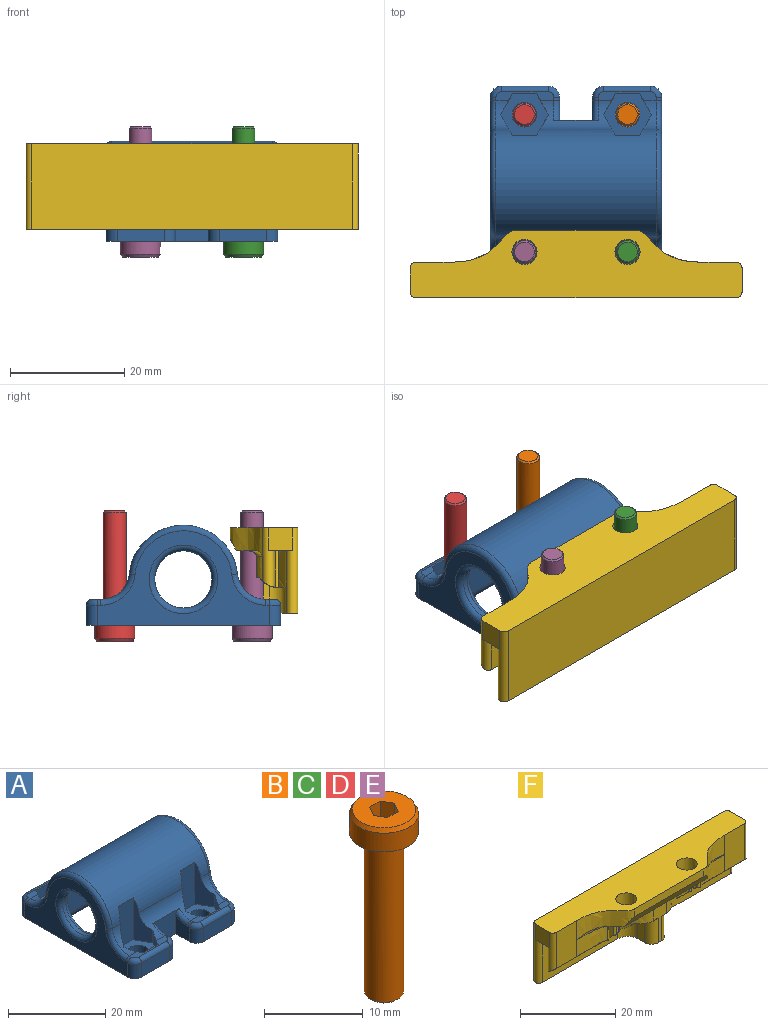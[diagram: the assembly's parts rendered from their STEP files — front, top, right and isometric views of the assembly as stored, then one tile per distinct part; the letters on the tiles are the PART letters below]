
ASSEMBLY  parts=6 mates=5
PART A: 114 faces, bbox 30.4x34.4x18.3 mm
  f0: cylinder r=2.15mm len=4.3mm, axis (0,0,-1), area 27mm2, adj f21,f94
  f1: cylinder r=2.15mm len=4.3mm, axis (0,0,-1), area 27mm2, adj f21,f95
  f2: cylinder r=2.15mm len=4.3mm, axis (0,0,-1), area 27mm2, adj f21,f108
  f3: cylinder r=2.15mm len=4.3mm, axis (0,0,-1), area 27mm2, adj f21,f81
  f4: cylinder r=5mm len=4.97mm, axis (-1,0,0), area 11.9mm2, adj f20,f22,f55,f103,f104
  f5: cylinder r=5mm len=4.97mm, axis (-1,0,0), area 11.9mm2, adj f9,f22,f70,f97,f98
  f6: cylinder r=5mm len=4.97mm, axis (-1,0,0), area 11.9mm2, adj f16,f22,f68,f89,f90
  f7: cylinder r=5mm len=4.97mm, axis (-1,0,0), area 11.9mm2, adj f8,f22,f53,f83,f84
  f8: plane 10.15x1.58mm, normal (0,0,1), area 9.5mm2, adj f7,f46,f48,f49,f50,f51,f52,f84
  f9: plane 10.15x1.58mm, normal (0,0,1), area 9.5mm2, adj f5,f45,f71,f72,f73,f74,f75,f98
  f10: plane 8.15x3.5mm, normal (0,-1,0), area 28.5mm2, adj f21,f33,f42,f73
  f11: plane 8.15x3.5mm, normal (0,1,0), area 28.5mm2, adj f21,f36,f43,f65
  f12: plane 24.2x6mm, normal (0,1,0), area 145.2mm2, adj f14,f24,f26,f39
  f13: plane 24.2x6mm, normal (0,-1,0), area 145.2mm2, adj f14,f24,f26,f38
  f14: cylinder r=7.55mm len=24.2mm, axis (-1,0,0), area 446.8mm2, adj f12,f13,f24,f26,f109,f110,f112,f113
  f15: plane 30x16.5mm, normal (-1,0,0), area 196.5mm2, adj f21,f41,f44,f52,f53,f54,f55,f56
  f16: plane 10.15x1.58mm, normal (0,0,1), area 9.5mm2, adj f6,f46,f63,f64,f65,f66,f67,f90
  f17: plane 8.15x3.5mm, normal (0,-1,0), area 28.5mm2, adj f21,f34,f41,f58
  f18: plane 30x16.5mm, normal (1,0,0), area 196.5mm2, adj f21,f42,f43,f67,f68,f69,f70,f71
  f19: plane 8.15x3.5mm, normal (0,1,0), area 28.5mm2, adj f21,f35,f44,f50
  f20: plane 10.15x1.58mm, normal (0,0,1), area 9.5mm2, adj f4,f45,f56,f57,f58,f59,f60,f104
  f21: plane 34x30mm, normal (0,0,-1), area 348mm2, adj f0,f1,f2,f3,f10,f11,f15,f17
  f22: cylinder r=9.5mm len=28mm, axis (-1,0,0), area 706mm2, adj f4,f5,f6,f7,f45,f46,f54,f69
  f23: cylinder r=5mm len=10mm, axis (-1,0,0), area 28.3mm2, adj f79,f80
  f24: plane 15.1x13.55mm, normal (1,0,0), area 67mm2, adj f12,f13,f14,f37,f80
  f25: cylinder r=5mm len=10mm, axis (1,0,0), area 28.3mm2, adj f77,f78
  f26: plane 15.1x13.55mm, normal (-1,0,0), area 67mm2, adj f12,f13,f14,f40,f77
  f27: plane 4.57x4mm, normal (-1,0,0), area 15.2mm2, adj f21,f28,f33,f75,f76
  f28: plane 7.7x5.85mm, normal (0,-1,0), area 33.9mm2, adj f21,f27,f29,f45,f61,f76
  f29: plane 4.57x4mm, normal (1,0,0), area 15.2mm2, adj f21,f28,f34,f60,f61
  f30: plane 4.57x4mm, normal (1,0,0), area 15.2mm2, adj f21,f31,f35,f47,f48
  f31: plane 7.7x5.85mm, normal (0,1,0), area 33.9mm2, adj f21,f30,f32,f46,f47,f62
  f32: plane 4.57x4mm, normal (-1,0,0), area 15.2mm2, adj f21,f31,f36,f62,f63
  f33: cylinder r=2mm len=3.5mm, axis (0,0,1), area 11mm2, adj f10,f21,f27,f74
  f34: cylinder r=2mm len=3.5mm, axis (0,0,-1), area 11mm2, adj f17,f21,f29,f59
  f35: cylinder r=2mm len=3.5mm, axis (0,0,-1), area 11mm2, adj f19,f21,f30,f49
  f36: cylinder r=2mm len=3.5mm, axis (0,0,1), area 11mm2, adj f11,f21,f32,f64
  f37: cylinder r=2mm len=19.1mm, axis (0,-1,0), area 52mm2, adj f21,f24,f38,f39
  f38: cylinder r=2mm len=28.2mm, axis (-1,0,0), area 80.6mm2, adj f13,f21,f37,f40
  f39: cylinder r=2mm len=28.2mm, axis (1,0,0), area 80.6mm2, adj f12,f21,f37,f40
  f40: cylinder r=2mm len=19.1mm, axis (0,-1,0), area 52mm2, adj f21,f26,f38,f39
  f41: cylinder r=2mm len=3.5mm, axis (0,0,-1), area 11mm2, adj f15,f17,f21,f57
  f42: cylinder r=2mm len=3.5mm, axis (0,0,1), area 11mm2, adj f10,f18,f21,f72
  f43: cylinder r=2mm len=3.5mm, axis (0,0,-1), area 11mm2, adj f11,f18,f21,f66
  f44: cylinder r=2mm len=3.5mm, axis (0,0,1), area 11mm2, adj f15,f19,f21,f51
  f45: cylinder r=5mm len=12.52mm, axis (-1,0,0), area 53.5mm2, adj f9,f20,f22,f28,f61,f76,f100,f101
  f46: cylinder r=5mm len=12.52mm, axis (-1,0,0), area 53.5mm2, adj f8,f16,f22,f31,f47,f62,f86,f87
  f47: torus R=6mm, axis (-1,0,0), area 5.8mm2, adj f30,f31,f46,f48
  f48: cylinder r=1mm len=1mm, axis (0,1,0), area 0.9mm2, adj f8,f30,f47,f49
  f49: torus R=1mm, axis (0,0,1), area 4mm2, adj f8,f35,f48,f50
  f50: cylinder r=1mm len=8.15mm, axis (1,0,0), area 12.8mm2, adj f8,f19,f49,f51
  f51: torus R=1mm, axis (0,0,1), area 4mm2, adj f8,f44,f50,f52
  f52: cylinder r=1mm len=1mm, axis (0,1,0), area 0.9mm2, adj f8,f15,f51,f53
  f53: torus R=6mm, axis (1,0,0), area 12.4mm2, adj f7,f15,f52,f54
  f54: torus R=8.5mm, axis (1,0,0), area 42.1mm2, adj f15,f22,f53,f55
  f55: torus R=6mm, axis (1,0,0), area 12.4mm2, adj f4,f15,f54,f56
  f56: cylinder r=1mm len=1mm, axis (0,1,0), area 0.9mm2, adj f15,f20,f55,f57
  f57: torus R=1mm, axis (0,0,1), area 4mm2, adj f20,f41,f56,f58
  f58: cylinder r=1mm len=8.15mm, axis (-1,0,0), area 12.8mm2, adj f17,f20,f57,f59
  f59: torus R=1mm, axis (0,0,1), area 4mm2, adj f20,f34,f58,f60
  f60: cylinder r=1mm len=1mm, axis (0,1,0), area 0.9mm2, adj f20,f29,f59,f61
  f61: torus R=6mm, axis (1,0,0), area 5.8mm2, adj f28,f29,f45,f60
  f62: torus R=6mm, axis (-1,0,0), area 5.8mm2, adj f31,f32,f46,f63
  f63: cylinder r=1mm len=1mm, axis (0,-1,0), area 0.9mm2, adj f16,f32,f62,f64
  f64: torus R=1mm, axis (0,0,1), area 4mm2, adj f16,f36,f63,f65
  f65: cylinder r=1mm len=8.15mm, axis (1,0,0), area 12.8mm2, adj f11,f16,f64,f66
  f66: torus R=1mm, axis (0,0,1), area 4mm2, adj f16,f43,f65,f67
  f67: cylinder r=1mm len=1mm, axis (0,-1,0), area 0.9mm2, adj f16,f18,f66,f68
  f68: torus R=6mm, axis (1,0,0), area 12.4mm2, adj f6,f18,f67,f69
  f69: torus R=8.5mm, axis (1,0,0), area 42.1mm2, adj f18,f22,f68,f70
  f70: torus R=6mm, axis (1,0,0), area 12.4mm2, adj f5,f18,f69,f71
  f71: cylinder r=1mm len=1mm, axis (0,-1,0), area 0.9mm2, adj f9,f18,f70,f72
  f72: torus R=1mm, axis (0,0,1), area 4mm2, adj f9,f42,f71,f73
  f73: cylinder r=1mm len=8.15mm, axis (-1,0,0), area 12.8mm2, adj f9,f10,f72,f74
  f74: torus R=1mm, axis (0,0,1), area 4mm2, adj f9,f33,f73,f75
  f75: cylinder r=1mm len=1mm, axis (0,-1,0), area 0.9mm2, adj f9,f27,f74,f76
  f76: torus R=6mm, axis (1,0,0), area 5.8mm2, adj f27,f28,f45,f75
  f77: torus R=6mm, axis (1,0,0), area 52.9mm2, adj f25,f26
  f78: torus R=6mm, axis (1,0,0), area 52.9mm2, adj f18,f25
  f79: torus R=6mm, axis (1,0,0), area 52.9mm2, adj f15,f23
  f80: torus R=6mm, axis (-1,0,0), area 52.9mm2, adj f23,f24
  f81: plane 8.43x7.3mm, normal (0,0,1), area 31.6mm2, adj f3,f82,f83,f84,f85,f86,f87
  f82: plane 10.53x4.21mm, normal (0,1,0), area 44.4mm2, adj f22,f81,f83,f87
  f83: plane 10.53x3.65mm, normal (0.87,0.5,0), area 24.5mm2, adj f7,f22,f81,f82,f84
  f84: plane 3.7x3.17mm, normal (0.87,-0.5,0), area 11.1mm2, adj f7,f8,f81,f83,f85
  f85: plane 4.21x2.5mm, normal (0,-1,0), area 10.5mm2, adj f8,f81,f84,f86
  f86: plane 3.7x3.17mm, normal (-0.87,-0.5,0), area 11.1mm2, adj f8,f46,f81,f85,f87
  f87: plane 10.53x3.65mm, normal (-0.87,0.5,0), area 24.5mm2, adj f22,f46,f81,f82,f86
  f88: plane 10.53x4.21mm, normal (0,1,0), area 44.4mm2, adj f22,f89,f93,f94
  f89: plane 10.53x3.65mm, normal (-0.87,0.5,0), area 24.5mm2, adj f6,f22,f88,f90,f94
  f90: plane 3.7x3.17mm, normal (-0.87,-0.5,0), area 11.1mm2, adj f6,f16,f89,f91,f94
  f91: plane 4.21x2.5mm, normal (0,-1,0), area 10.5mm2, adj f16,f90,f92,f94
  f92: plane 3.7x3.17mm, normal (0.87,-0.5,0), area 11.1mm2, adj f16,f46,f91,f93,f94
  f93: plane 10.53x3.65mm, normal (0.87,0.5,0), area 24.5mm2, adj f22,f46,f88,f92,f94
  f94: plane 8.43x7.3mm, normal (0,0,1), area 31.6mm2, adj f0,f88,f89,f90,f91,f92,f93
  f95: plane 8.43x7.3mm, normal (0,0,1), area 31.6mm2, adj f1,f96,f97,f98,f99,f100,f101
  f96: plane 10.53x4.21mm, normal (0,-1,0), area 44.4mm2, adj f22,f95,f97,f101
  f97: plane 10.53x3.65mm, normal (-0.87,-0.5,0), area 24.5mm2, adj f5,f22,f95,f96,f98
  f98: plane 3.7x3.17mm, normal (-0.87,0.5,0), area 11.1mm2, adj f5,f9,f95,f97,f99
  f99: plane 4.21x2.5mm, normal (0,1,0), area 10.5mm2, adj f9,f95,f98,f100
  f100: plane 3.7x3.17mm, normal (0.87,0.5,0), area 11.1mm2, adj f9,f45,f95,f99,f101
  f101: plane 10.53x3.65mm, normal (0.87,-0.5,0), area 24.5mm2, adj f22,f45,f95,f96,f100
  f102: plane 10.53x4.21mm, normal (0,-1,0), area 44.4mm2, adj f22,f103,f107,f108
  f103: plane 10.53x3.65mm, normal (0.87,-0.5,0), area 24.5mm2, adj f4,f22,f102,f104,f108
  f104: plane 3.7x3.17mm, normal (0.87,0.5,0), area 11.1mm2, adj f4,f20,f103,f105,f108
  f105: plane 4.21x2.5mm, normal (0,1,0), area 10.5mm2, adj f20,f104,f106,f108
  f106: plane 3.7x3.17mm, normal (-0.87,0.5,0), area 11.1mm2, adj f20,f45,f105,f107,f108
  f107: plane 10.53x3.65mm, normal (-0.87,-0.5,0), area 24.5mm2, adj f22,f45,f102,f106,f108
  f108: plane 8.43x7.3mm, normal (0,0,1), area 31.6mm2, adj f2,f102,f103,f104,f105,f106,f107
  f109: plane 5.64x1mm, normal (1,0,0), area 2.9mm2, adj f14,f111,f112,f113
  f110: plane 5.64x1mm, normal (-1,0,0), area 2.9mm2, adj f14,f111,f112,f113
  f111: plane 22x4.3mm, normal (0,0,-1), area 94.5mm2, adj f109,f110,f112,f113
  f112: plane 22x1mm, normal (0,-0.83,-0.56), area 26.5mm2, adj f14,f109,f110,f111
  f113: plane 22x1mm, normal (0,0.83,-0.56), area 26.5mm2, adj f14,f109,f110,f111
PART B: 19 faces, bbox 7x7x22.8 mm
  f0: plane 6.43x6.43mm, normal (0,0,1), area 26.7mm2, adj f3,f10,f11,f12,f13,f14,f15
  f1: cylinder r=3.5mm len=7mm, axis (0,0,-1), area 50.8mm2, adj f2,f3
  f2: plane 7x7mm, normal (0,0,-1), area 26mm2, adj f1,f16
  f3: cone r=3.5mm half-angle=30deg, axis (0,0,-1), area 11.9mm2, adj f0,f1
  f4: plane 1.5x1.3mm, normal (-0.15,0.09,0.98), area 1mm2, adj f5,f9,f12
  f5: plane 1.5x1.3mm, normal (0,0.17,0.98), area 1mm2, adj f4,f6,f13
  f6: plane 1.5x1.3mm, normal (0.15,0.09,0.98), area 1mm2, adj f5,f7,f14
  f7: plane 1.5x1.3mm, normal (0.15,-0.09,0.98), area 1mm2, adj f6,f8,f15
  f8: plane 1.5x1.3mm, normal (0,-0.17,0.98), area 1mm2, adj f7,f9,f10
  f9: plane 1.5x1.3mm, normal (-0.15,-0.09,0.98), area 1mm2, adj f4,f8,f11
  f10: plane 2.3x1.5mm, normal (0,-1,0), area 3.4mm2, adj f0,f8,f11,f15
  f11: plane 2.3x1.3mm, normal (-0.87,-0.5,0), area 3.4mm2, adj f0,f9,f10,f12
  f12: plane 2.3x1.3mm, normal (-0.87,0.5,0), area 3.4mm2, adj f0,f4,f11,f13
  f13: plane 2.3x1.5mm, normal (0,1,0), area 3.4mm2, adj f0,f5,f12,f14
  f14: plane 2.3x1.3mm, normal (0.87,0.5,0), area 3.4mm2, adj f0,f6,f13,f15
  f15: plane 2.3x1.3mm, normal (0.87,-0.5,0), area 3.4mm2, adj f0,f7,f10,f14
  f16: cylinder r=1.99mm len=19.72mm, axis (0,0,1), area 246.6mm2, adj f2,f18
  f17: plane 3.42x3.42mm, normal (0,0,-1), area 9.2mm2, adj f18
  f18: cone r=1.71mm half-angle=45deg, axis (0,0,1), area 4.6mm2, adj f16,f17
PART C: same geometry as B
PART D: same geometry as B
PART E: same geometry as B
PART F: 67 faces, bbox 58.7x12.7x15.7 mm
  f0: plane 10.22x1.42mm, normal (0,0,-1), area 8.7mm2, adj f10,f18,f32,f34
  f1: extruded ~6.45x2.8mm, area 17.8mm2, adj f13,f15,f16,f27,f28
  f2: cylinder r=2.2mm len=9.65mm, axis (0,0,1), area 66.9mm2, adj f14,f15,f16,f27,f28,f66
  f3: extruded ~6.5x3.62mm, area 25.8mm2, adj f13,f14,f16,f28
  f4: extruded ~9.29x8.21mm, area 34mm2, adj f9,f12,f20,f23,f29,f30,f66
  f5: plane 6.1x2.21mm, normal (0.93,0.38,0), area 9mm2, adj f6,f12,f16,f24,f29,f30
  f6: extruded ~6.4x2.36mm, area 16.6mm2, adj f5,f7,f16,f30
  f7: plane 11.81x6.4mm, normal (0,1,0), area 75.6mm2, adj f6,f11,f16,f30
  f8: plane 4.2x4mm, normal (-1,0,0), area 16.8mm2, adj f11,f16,f22,f66
  f9: plane 9.29x6mm, normal (0,-1,0), area 55.7mm2, adj f4,f11,f30,f66
  f10: extruded ~11.23x7mm, area 77mm2, adj f0,f16,f18,f19,f31,f32
  f11: cylinder r=1mm len=10.4mm, axis (0,0,-1), area 24.9mm2, adj f7,f8,f9,f16,f30,f66
  f12: cylinder r=0.4mm len=3.69mm, axis (0,0,1), area 3.6mm2, adj f4,f5,f24,f29
  f13: cylinder r=0.4mm len=6.5mm, axis (0,0,1), area 5.8mm2, adj f1,f3,f16,f28
  f14: cylinder r=0.4mm len=6.09mm, axis (0,0,1), area 5.6mm2, adj f2,f3,f16,f28
  f15: cylinder r=0.4mm len=4.69mm, axis (0,0,1), area 4.3mm2, adj f1,f2,f16,f27
  f16: plane 58.09x9.99mm, normal (0,0,-1), area 164.3mm2, adj f1,f2,f3,f5,f6,f7,f8,f10
  f17: plane 56x15mm, normal (0,1,0), area 840mm2, adj f22,f26,f54,f66
  f18: plane 22.5x11mm, normal (0,-1,0), area 197.3mm2, adj f0,f10,f16,f22,f26,f34
  f19: plane 11x4mm, normal (0,-1,0), area 25.1mm2, adj f10,f16,f26,f31,f35,f46,f62,f65
  f20: extruded ~11.68x5.6mm, area 55mm2, adj f4,f16,f21,f23,f33,f66
  f21: plane 20.63x2mm, normal (0,-1,0), area 41.3mm2, adj f20,f33,f53,f66
  f22: cylinder r=1mm len=15mm, axis (0,0,1), area 40.8mm2, adj f8,f16,f17,f18,f26,f66
  f23: bspline ~13.56x5.87mm, area 10.1mm2, adj f4,f16,f20,f24
  f24: bspline ~3.37x1.88mm, area 1.8mm2, adj f5,f12,f16,f23
  f25: plane 6.31x2mm, normal (-1,0,0), area 11.2mm2, adj f26,f31,f32,f34,f35
  f26: plane 58x9mm, normal (0,0,-1), area 152.3mm2, adj f17,f18,f19,f22,f25,f34,f35,f52
  f27: plane 0.87x0.36mm, normal (0,0,-1), area 0.2mm2, adj f1,f2,f15,f28
  f28: cylinder r=4mm len=4.04mm, axis (1,0,0), area 10mm2, adj f1,f2,f3,f13,f14,f27
  f29: plane 1.98x0.58mm, normal (0,0,-1), area 0.6mm2, adj f4,f5,f12,f30
  f30: cylinder r=4mm len=15.76mm, axis (1,0,0), area 37.1mm2, adj f4,f5,f6,f7,f9,f11,f29
  f31: plane 5.2x2.55mm, normal (0,0,-1), area 5.1mm2, adj f10,f19,f25,f32,f35
  f32: cylinder r=4mm len=6.45mm, axis (1,0,0), area 18.5mm2, adj f0,f10,f25,f31,f34
  f33: plane 25.5x2.66mm, normal (0,-0.89,-0.45), area 52.5mm2, adj f16,f20,f21,f53
  f34: cylinder r=3mm len=4.86mm, axis (0,0,1), area 21.5mm2, adj f0,f18,f25,f26,f32
  f35: cylinder r=2mm len=6.31mm, axis (0,0,-1), area 19.8mm2, adj f19,f25,f26,f31
  f36: plane 10.22x1.42mm, normal (0,0,-1), area 8.7mm2, adj f46,f52,f63,f64
  f37: extruded ~6.45x2.8mm, area 17.8mm2, adj f16,f49,f51,f58,f59
  f38: cylinder r=2.2mm len=9.65mm, axis (0,0,1), area 66.9mm2, adj f16,f50,f51,f58,f59,f66
  f39: extruded ~6.5x3.62mm, area 25.8mm2, adj f16,f49,f50,f59
  f40: extruded ~9.29x8.21mm, area 34mm2, adj f45,f48,f53,f55,f60,f61,f66
  f41: plane 6.1x2.21mm, normal (-0.93,0.38,0), area 9mm2, adj f16,f42,f48,f56,f60,f61
  f42: extruded ~6.4x2.36mm, area 16.6mm2, adj f16,f41,f43,f61
  f43: plane 11.81x6.4mm, normal (0,1,0), area 75.6mm2, adj f16,f42,f47,f61
  f44: plane 4.2x4mm, normal (1,0,0), area 16.8mm2, adj f16,f47,f54,f66
  f45: plane 9.29x6mm, normal (0,-1,0), area 55.7mm2, adj f40,f47,f61,f66
  f46: extruded ~11.23x7mm, area 77mm2, adj f16,f19,f36,f52,f62,f63
  f47: cylinder r=1mm len=10.4mm, axis (0,0,-1), area 24.9mm2, adj f16,f43,f44,f45,f61,f66
  f48: cylinder r=0.4mm len=3.69mm, axis (0,0,1), area 3.6mm2, adj f40,f41,f56,f60
  f49: cylinder r=0.4mm len=6.5mm, axis (0,0,1), area 5.8mm2, adj f16,f37,f39,f59
  f50: cylinder r=0.4mm len=6.09mm, axis (0,0,1), area 5.6mm2, adj f16,f38,f39,f59
  f51: cylinder r=0.4mm len=4.69mm, axis (0,0,1), area 4.3mm2, adj f16,f37,f38,f58
  f52: plane 22.5x11mm, normal (0,-1,0), area 197.3mm2, adj f16,f26,f36,f46,f54,f64
  f53: extruded ~11.68x5.6mm, area 55mm2, adj f16,f21,f33,f40,f55,f66
  f54: cylinder r=1mm len=15mm, axis (0,0,1), area 40.8mm2, adj f16,f17,f26,f44,f52,f66
  f55: bspline ~13.56x5.87mm, area 10.1mm2, adj f16,f40,f53,f56
  f56: bspline ~3.37x1.88mm, area 1.8mm2, adj f16,f41,f48,f55
  f57: plane 6.31x2mm, normal (1,0,0), area 11.2mm2, adj f26,f62,f63,f64,f65
  f58: plane 0.87x0.36mm, normal (0,0,-1), area 0.2mm2, adj f37,f38,f51,f59
  f59: cylinder r=4mm len=4.04mm, axis (-1,0,0), area 10mm2, adj f37,f38,f39,f49,f50,f58
  f60: plane 1.98x0.58mm, normal (0,0,-1), area 0.6mm2, adj f40,f41,f48,f61
  f61: cylinder r=4mm len=15.76mm, axis (-1,0,0), area 37.1mm2, adj f40,f41,f42,f43,f45,f47,f60
  f62: plane 5.2x2.55mm, normal (0,0,-1), area 5.1mm2, adj f19,f46,f57,f63,f65
  f63: cylinder r=4mm len=6.45mm, axis (-1,0,0), area 18.5mm2, adj f36,f46,f57,f62,f64
  f64: cylinder r=3mm len=4.86mm, axis (0,0,1), area 21.5mm2, adj f26,f36,f52,f57,f63
  f65: cylinder r=2mm len=6.31mm, axis (0,0,-1), area 19.8mm2, adj f19,f26,f57,f62
  f66: plane 58x11.8mm, normal (0,0,1), area 490.4mm2, adj f2,f4,f8,f9,f11,f17,f20,f21
PLACE A at identity
PLACE B rot(axis=(1,0,0),180deg) t=(9,12,-2.8)mm
PLACE C rot(axis=(1,0,0),180deg) t=(9,-12,-2.8)mm
PLACE D rot(axis=(1,0,0),180deg) t=(-9,12,-2.8)mm
PLACE E rot(axis=(1,0,0),180deg) t=(-9,-12,-2.8)mm
PLACE F rot(axis=(0,0,1),180deg) t=(0,-12,13.05)mm
MATE slider F.f2 <-> C.f1  axis (0,0,-1) through (9,-12,13.05)mm
MATE fastened B.f1 <-> A.f0  axis (0,0,1) through (9,12,0)mm
MATE fastened E.f1 <-> A.f2  axis (0,0,1) through (-9,-12,0)mm
MATE fastened D.f1 <-> A.f3  axis (0,0,1) through (-9,12,0)mm
MATE fastened C.f1 <-> A.f1  axis (0,0,1) through (9,-12,0)mm
